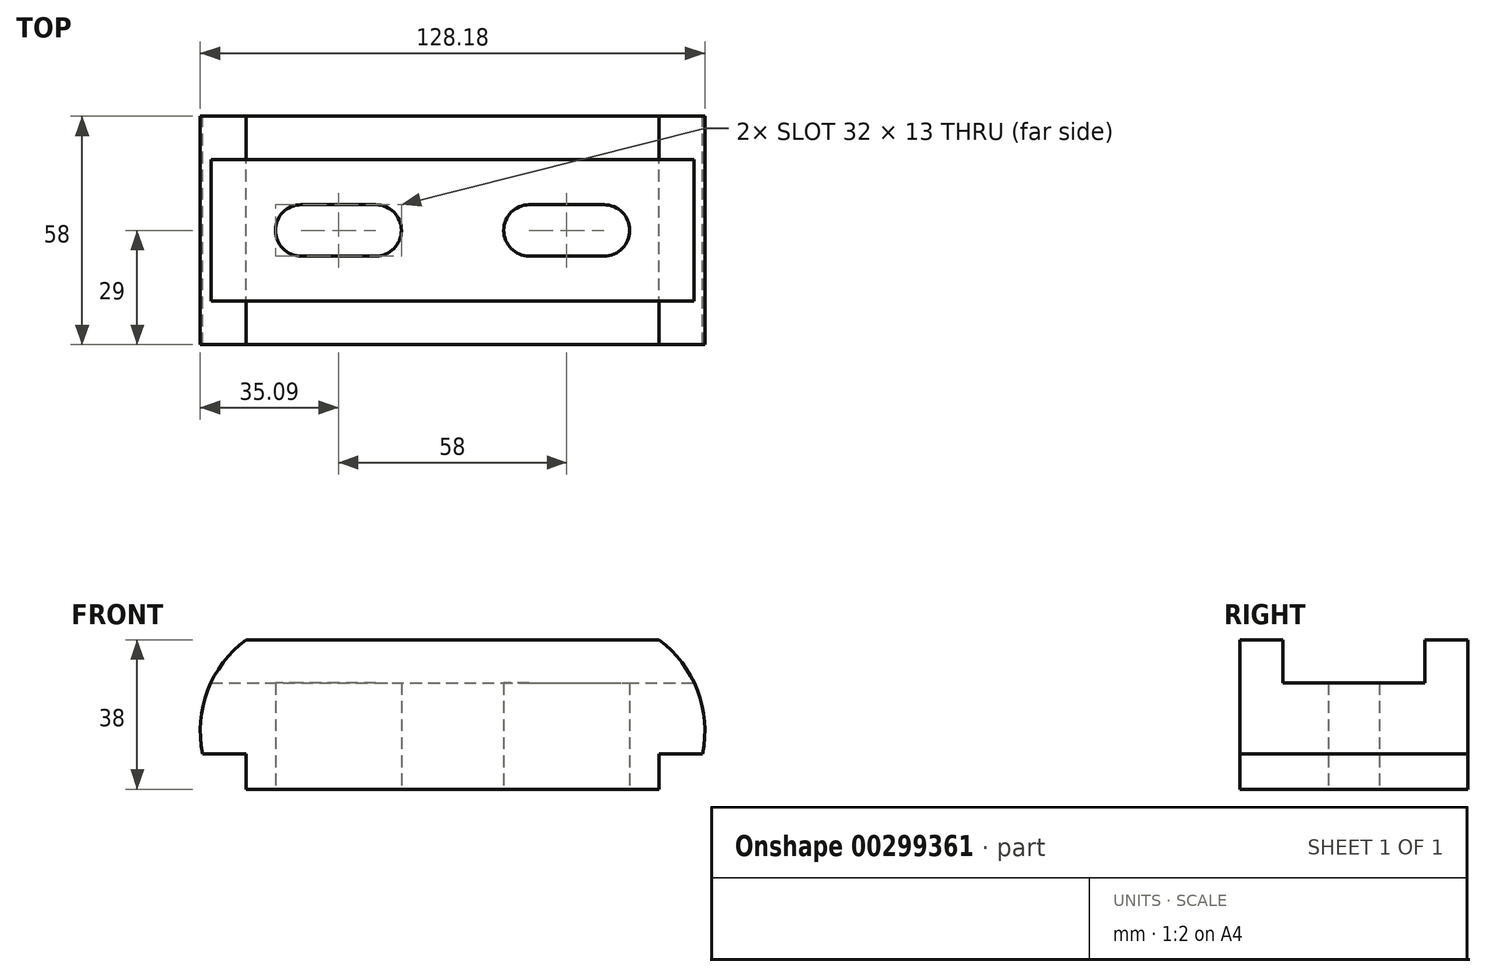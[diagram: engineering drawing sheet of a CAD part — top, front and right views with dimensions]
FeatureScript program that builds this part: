
annotation { "Feature Type Name" : "Feature", "Feature Type Description" : "" }
export const myFeature = defineFeature(function(context is Context, id is Id, definition is map)
    precondition{}
    {
        {
            var Q0;
            Q0=qCreatedBy(makeId("Front.planeOp"),FACE);
            var sketch = newSketch(context, id + "F0", { "sketchPlane" : qUnion([Q0])});
            skLineSegment(sketch, "E0", {"start": v(0, 0) * mm, "end": v(52.5, 0) * mm});
            skLineSegment(sketch, "E1", {"start": v(52.5, 0) * mm, "end": v(52.5, 9) * mm});
            skLineSegment(sketch, "E2", {"start": v(52.5, 9) * mm, "end": v(63.5, 9) * mm});
            skArc(sketch, "E3", {"start": v(63.5, 9) * mm, "mid": v(62.2, 25.1) * mm, "end": v(52.5, 38) * mm});
            skLineSegment(sketch, "E4", {"start": v(52.5, 38) * mm, "end": v(0, 38) * mm});
            skArc(sketch, "E5.MirrorCS", {"start": v(-63.5, 9) * mm, "mid": v(-62.2, 25.1) * mm, "end": v(-52.5, 38) * mm});
            skLineSegment(sketch, "E6.MirrorCS", {"start": v(-52.5, 9) * mm, "end": v(-63.5, 9) * mm});
            skLineSegment(sketch, "E7.MirrorCS", {"start": v(-52.5, 0) * mm, "end": v(-52.5, 9) * mm});
            skLineSegment(sketch, "E8.MirrorCS", {"start": v(-52.5, 38) * mm, "end": v(0, 38) * mm});
            skLineSegment(sketch, "E9.MirrorCS", {"start": v(0, 0) * mm, "end": v(-52.5, 0) * mm});
            skSolve(sketch);
        }
        {
            var Q0;
            Q0 = qSketchRegion(id + "F0", true);
            extrude(context, id + "F1", {"entities" : qUnion([Q0]), "endBound" : BoundingType.SYMMETRIC, "depth" : 58 * mm});
        }
        {
            var Q0;
            Q0=makeQuery(id+"F1.opExtrude","SWEPT_FACE",FACE,{"disambiguationData":[OSD([sQuery(id+"F0.wireOp",EDGE,"E4"),sQuery(id+"F0.wireOp",EDGE,"E8.MirrorCS")])]});
            var sketch = newSketch(context, id + "F2", { "sketchPlane" : qUnion([Q0])});
            skLineSegment(sketch, "E10.bottom", {"start": v(-62.2, 18) * mm, "end": v(62.2, 18) * mm});
            skLineSegment(sketch, "E10.top", {"start": v(-62.2, -18) * mm, "end": v(62.2, -18) * mm});
            skLineSegment(sketch, "E10.left", {"start": v(-62.2, 18) * mm, "end": v(-62.2, -18) * mm});
            skLineSegment(sketch, "E10.right", {"start": v(62.2, 18) * mm, "end": v(62.2, -18) * mm});
            skSolve(sketch);
        }
        {
            var Q0;
            Q0 = qSketchRegion(id + "F2", true);
            extrude(context, id + "F3", {"entities" : qUnion([Q0]), "operationType" : NewBodyOperationType.REMOVE, "oppositeDirection" : true, "depth" : 11 * mm});
        }
        {
            var Q0;
            Q0=qCreatedBy(makeId("Top.planeOp"),FACE);
            var sketch = newSketch(context, id + "F4", { "sketchPlane" : qUnion([Q0])});
            skLineSegment(sketch, "E11", {"start": v(-38.5, 6.5) * mm, "end": v(-19.5, 6.5) * mm});
            skArc(sketch, "E12", {"start": v(-19.5, -6.5) * mm, "mid": v(-13, 0) * mm, "end": v(-19.5, 6.5) * mm});
            skLineSegment(sketch, "E13", {"start": v(-19.5, -6.5) * mm, "end": v(-38.5, -6.5) * mm});
            skArc(sketch, "E14", {"start": v(-38.5, 6.5) * mm, "mid": v(-45, 0) * mm, "end": v(-38.5, -6.5) * mm});
            skArc(sketch, "E15.MirrorCS", {"start": v(19.5, -6.5) * mm, "mid": v(13, 0) * mm, "end": v(19.5, 6.5) * mm});
            skLineSegment(sketch, "E16.MirrorCS", {"start": v(38.5, 6.5) * mm, "end": v(19.5, 6.5) * mm});
            skArc(sketch, "E17.MirrorCS", {"start": v(38.5, 6.5) * mm, "mid": v(45, 0) * mm, "end": v(38.5, -6.5) * mm});
            skLineSegment(sketch, "E18.MirrorCS", {"start": v(19.5, -6.5) * mm, "end": v(38.5, -6.5) * mm});
            skSolve(sketch);
        }
        {
            var Q0;
            Q0 = qSketchRegion(id + "F4", true);
            var Q1;
            Q1=makeQuery(id+"F3.boolean.opBoolean","COPY",FACE,{"derivedFrom":makeQuery(id+"F3.opExtrude","CAP_FACE",FACE,{"disambiguationData":[OSD([sQuery(id+"F2.wireOp",EDGE,"E10.bottom"),sQuery(id+"F2.wireOp",EDGE,"E10.top"),sQuery(id+"F2.wireOp",EDGE,"E10.left"),sQuery(id+"F2.wireOp",EDGE,"E10.right")])],"isStart":false})});
            extrude(context, id + "F5", {"entities" : qUnion([Q0]), "operationType" : NewBodyOperationType.REMOVE, "endBound" : BoundingType.THROUGH_ALL, "endBoundEntityFace" : qUnion([Q1]), "depth" : 13 * mm});
        }
    });
